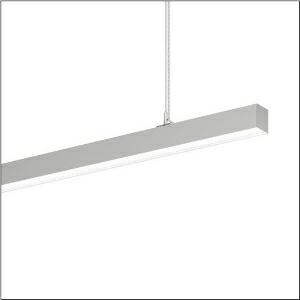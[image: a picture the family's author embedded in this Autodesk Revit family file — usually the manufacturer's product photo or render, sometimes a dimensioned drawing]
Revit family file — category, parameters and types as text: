
# Revit family: silica_r__21_51mx33tat7s_6391
name_source: partatom
category: Lighting Fixtures
units: mm (PartAtom-declared; Revit-internal decimal feet)

## family parameters
Cut with Voids When Loaded = No
Host = Face
Light Source = No
Part Type = Normal
Room Calculation Point = No
Round Connector Dimension = Use Diameter
Shared = No

## types (1)
- --- (1 x LED, 5740 lm, 53.8 W, 6500K)
    Apparent Load = 54 VA
    CIE Flux Codes = 78 96 99 56 100
    Color Rendering = 80
    Color Temperature = 6500K
    Default Elevation = 1800 mm
    Description = Silica® 21, office luminaire, primary optical cover: prismatic diffuser, of PMMA, CAT 2 (L<= 3000cd/m²), light emission: direct/indirect distribution, primary light characteristic: symmetric, installation type: suspended mounting, LED, rated luminous flux: 5.740lm, luminous efficacy: 102lm/W, light colour: 8tw, colour temperature: 2700..6500K, control gear: DALI DT8, with terminal, 3+2-pole, max. 2.5mm², mains connection: 220..240V, AC, 50/60Hz, rated input power: 56.5W, luminaire housing, of aluminium, metallic grey (RAL 9006), length: 1.204mm, width: 53mm, height: 53mm, protection rating (complete): IP20, insulation class (complete): insulation class I (protective earthing), certification: CE, permissible operating ambient temperature: 0..+35°C, standard: EN 50419, packaging unit: 1 piece
    Height = 53 mm
    Lamp = 1 x LED
    Lamp Light Flux = 5740 lm
    Lamp Power = 53.8 W
    Lamp count = 1
    Length = 1204 mm
    Luminous efficacy = 107 lm/W
    Manufacturer = Siteco
    ModVariant = No
    Model = 51MX33TAT7S
    Mounting Place = Ceiling
    Mounting Type = Pendant
    Number of Poles = 1
    OnlyDefault = Yes
    Power Factor = 1
    Product Name = Silica® 21
    Product group = office luminaire | ceiling pendant
    ProductGroupID = 904
    Protection Class = Protection class I
    Protection Degree = IP 20
    RLX_Detail_Level = 1
    RLX_Emergency_Light_Flux = 0 lm
    RLX_Emergency_Type = 0
    RLX_Emergency_Type_DB = No
    RlxData = <blob elided: 20209 chars, md5=8d10ae60>
    Socket = socket
    Standby Power = 0 W
    System Light Flux = 5740 lm
    System Power = 54 W
    Type Comments = individual setting
    Type Image = l_1335864.jpg
    URL = http://relux.com
    VarID = @adj_139746
    Voltage = 0 V
    Weight = 0.00 kg
    Width = 53 mm

## geometry (parser evidence)
native form markers: Blend x4, Sweep x11
no freeform markers — native parametric forms only
